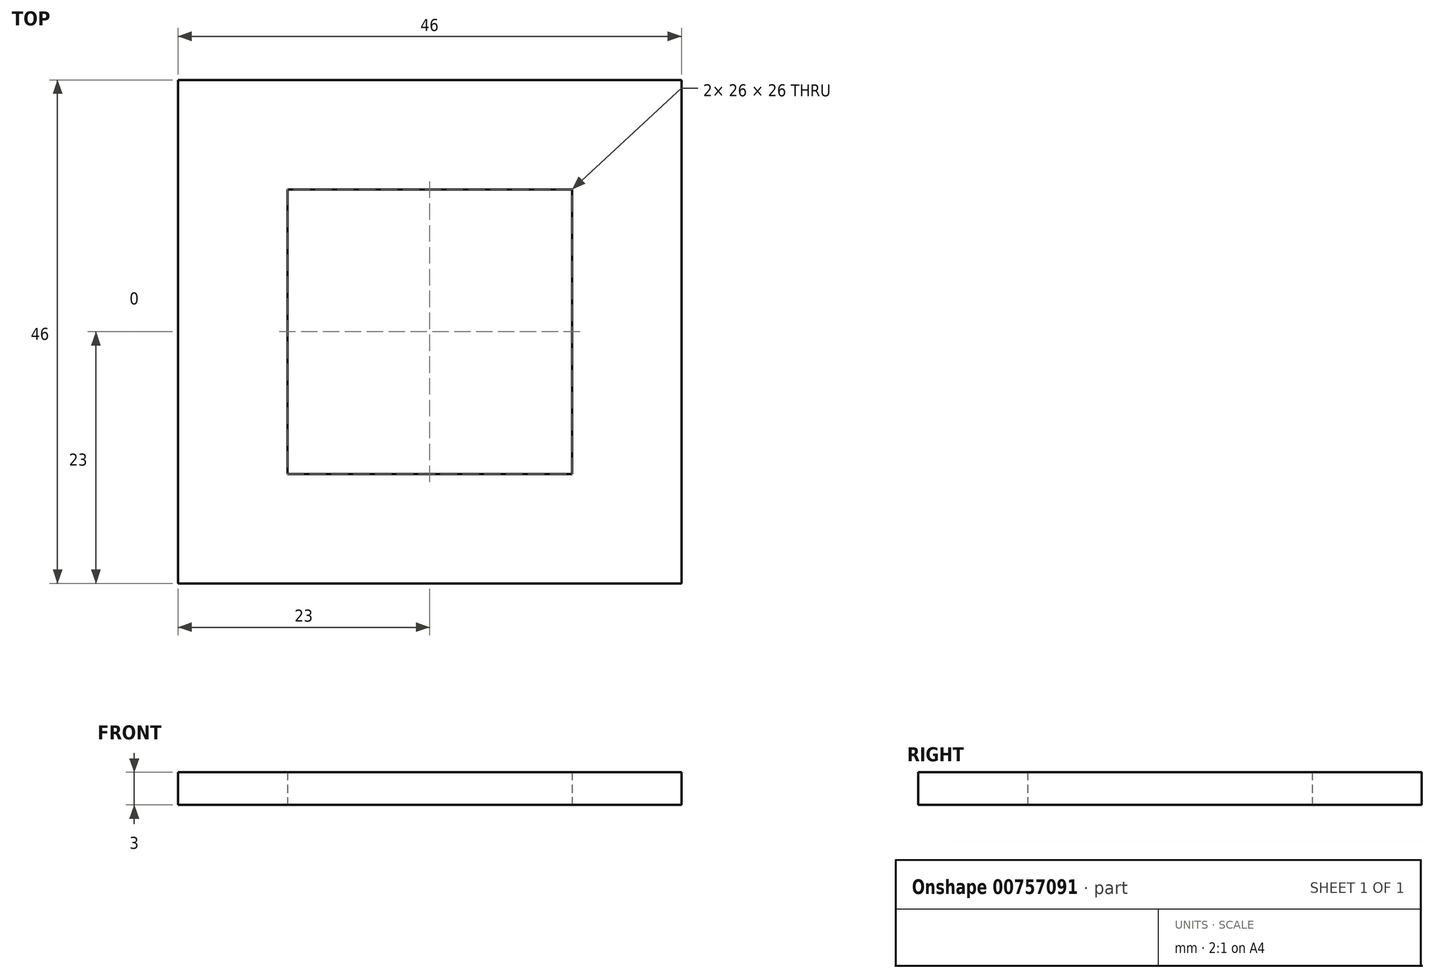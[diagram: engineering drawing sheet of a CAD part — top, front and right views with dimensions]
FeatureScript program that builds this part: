
annotation { "Feature Type Name" : "Feature", "Feature Type Description" : "" }
export const myFeature = defineFeature(function(context is Context, id is Id, definition is map)
    precondition{}
    {
        {
            var Q0;
            Q0=qCreatedBy(makeId("Top.planeOp"),FACE);
            var sketch = newSketch(context, id + "F0", { "sketchPlane" : qUnion([Q0])});
            skLineSegment(sketch, "E0.bottom", {"start": v(0, 0) * mm, "end": v(26, 0) * mm});
            skLineSegment(sketch, "E0.top", {"start": v(0, 26) * mm, "end": v(26, 26) * mm});
            skLineSegment(sketch, "E0.left", {"start": v(0, 0) * mm, "end": v(0, 26) * mm});
            skLineSegment(sketch, "E0.right", {"start": v(26, 0) * mm, "end": v(26, 26) * mm});
            skLineSegment(sketch, "E1.0", {"start": v(-10, 36) * mm, "end": v(36, 36) * mm});
            skLineSegment(sketch, "E1.1", {"start": v(-10, -10) * mm, "end": v(-10, 36) * mm});
            skLineSegment(sketch, "E1.2", {"start": v(-10, -10) * mm, "end": v(36, -10) * mm});
            skLineSegment(sketch, "E1.3", {"start": v(36, -10) * mm, "end": v(36, 36) * mm});
            skSolve(sketch);
        }
        {
            var Q0;
            Q0=makeQuery(id+"F0.imprint","IMPRINT",FACE,{"disambiguationData":[TD([[makeQuery(id+"F0.imprint","IMPRINT",EDGE,{"derivedFrom":sQuery(id+"F0.wireOp",EDGE,"E0.bottom")}),-1.0]])]});
            extrude(context, id + "F1", {"entities" : qUnion([Q0]), "depth" : 3 * mm, "offsetDistance" : 25 * mm});
        }
    });
